# Revit family: oventrop_hydrocontrol-vfn-1062456-58rfa
name_source: partatom
category: Арматура трубопроводов
revit_build: Autodesk Revit 2017 (Build: 20160225_1515(x64)
units: mm (PartAtom-declared; Revit-internal decimal feet)

## family parameters
Всегда вертикально = Да
Заголовок OmniClass = Adjusting/Controlling Valves for Liquid Services
На основе рабочей плоскости = Нет
Номер OmniClass = 23.65.55.14.17
Общий = Нет
При загрузке вырезать с полостями = Нет
Размер круглого соединителя = Использовать радиус
Тип детали = Клапан - Вставляется

## types (3) — shared parameters
Angle = 60.00°
Angle 2 = 30.00°
Angle 3 = -60.00°
Article Description = Balancing valve with both ports flanged
Article Type = Hydrocontrol VFN 10624 DN 200-300
Black = Color RGB 35-35-35
Bronze = Color RGB 156-122-90
Custom = Нет
EMCS Version = 2.0
ETIM Article Class = EC011463
Family Version = 10.14
Hb5 = 10 мм
Hlp1 = 56 мм
IFCExportAs = IfcValveType
IFCExportType = PRESSUREREDUCING
Lgt1 = 2 мм
MEPcontent Class = VALVE_BALANCING
Manufacturer URL = http://www.oventrop.de
Pressure Drop = 0.0 Па
Product Line = Oventrop
R1 = 9 мм
R2 = 10 мм
RegulatorRadius = 150 мм
Revit Version = 2015
r1 = 2 мм
r2 = 3 мм
Группа модели = Hydrocontrol VFN 10624 DN 200-300
Изготовитель = Oventrop
Описание = Balancing valve with both ports flanged

## per-type parameters (varying)
- DN 200: CurDst=67 мм; Dst1=68 мм; DstChk=68 мм; FlangeDiameter=340 мм; GTIN=4026755241167; H=473 мм; Hb1=460 мм; Hb2=290 мм; Hb3=48 мм; Hb4=110 мм; Hb6=218 мм; Height=467 мм; Hlp2=22 мм; K=295 мм; L2=67 мм; Length=600 мм; Lgt2=20 мм; Lgt3=59 мм; Lgt4=217 мм; Manufacturer Art. No.=1062456; NominalDiameter=200 мм; NominalRadius=100 мм; OuterDiameter=219 мм; Rad1=148 мм; Rad2=170 мм; Rad3=119 мм; Rad4=116 мм; Rad5=156 мм; Rad6=146 мм; Rad7=160 мм; URL=http://file-system.ru; VDst=54 мм; VHth=126 мм
- DN 250: CurDst=81 мм; Dst1=91 мм; DstChk=91 мм; FlangeDiameter=405 мм; GTIN=4026755241174; H=486 мм; Hb1=475 мм; Hb2=292 мм; Hb3=49 мм; Hb4=111 мм; Hb6=220 мм; Height=480 мм; Hlp2=27 мм; K=355 мм; L2=81 мм; Length=730 мм; Lgt2=22 мм; Lgt3=68 мм; Lgt4=260 мм; Manufacturer Art. No.=1062457; NominalDiameter=250 мм; NominalRadius=125 мм; OuterDiameter=273 мм; Rad1=178 мм; Rad2=203 мм; Rad3=143 мм; Rad4=140 мм; Rad5=180 мм; Rad6=170 мм; Rad7=184 мм; URL=www.stabiplan.com; VDst=63 мм; VHth=150 мм
- DN 300: CurDst=94 мм; Dst1=101 мм; DstChk=101 мм; FlangeDiameter=460 мм; GTIN=4026755241181; H=521 мм; Hb1=515 мм; Hb2=318 мм; Hb3=53 мм; Hb4=121 мм; Hb6=250 мм; Height=515 мм; Hlp2=31 мм; K=410 мм; L2=94 мм; Length=850 мм; Lgt2=23 мм; Lgt3=77 мм; Lgt4=302 мм; Manufacturer Art. No.=1062458; NominalDiameter=300 мм; NominalRadius=150 мм; OuterDiameter=324 мм; Rad1=205 мм; Rad2=230 мм; Rad3=166 мм; Rad4=163 мм; Rad5=203 мм; Rad6=193 мм; Rad7=207 мм; URL=www.stabiplan.com; VDst=72 мм; VHth=173 мм

## geometry (parser evidence)
native form markers: Blend x2, Sweep x2
no freeform markers — native parametric forms only
